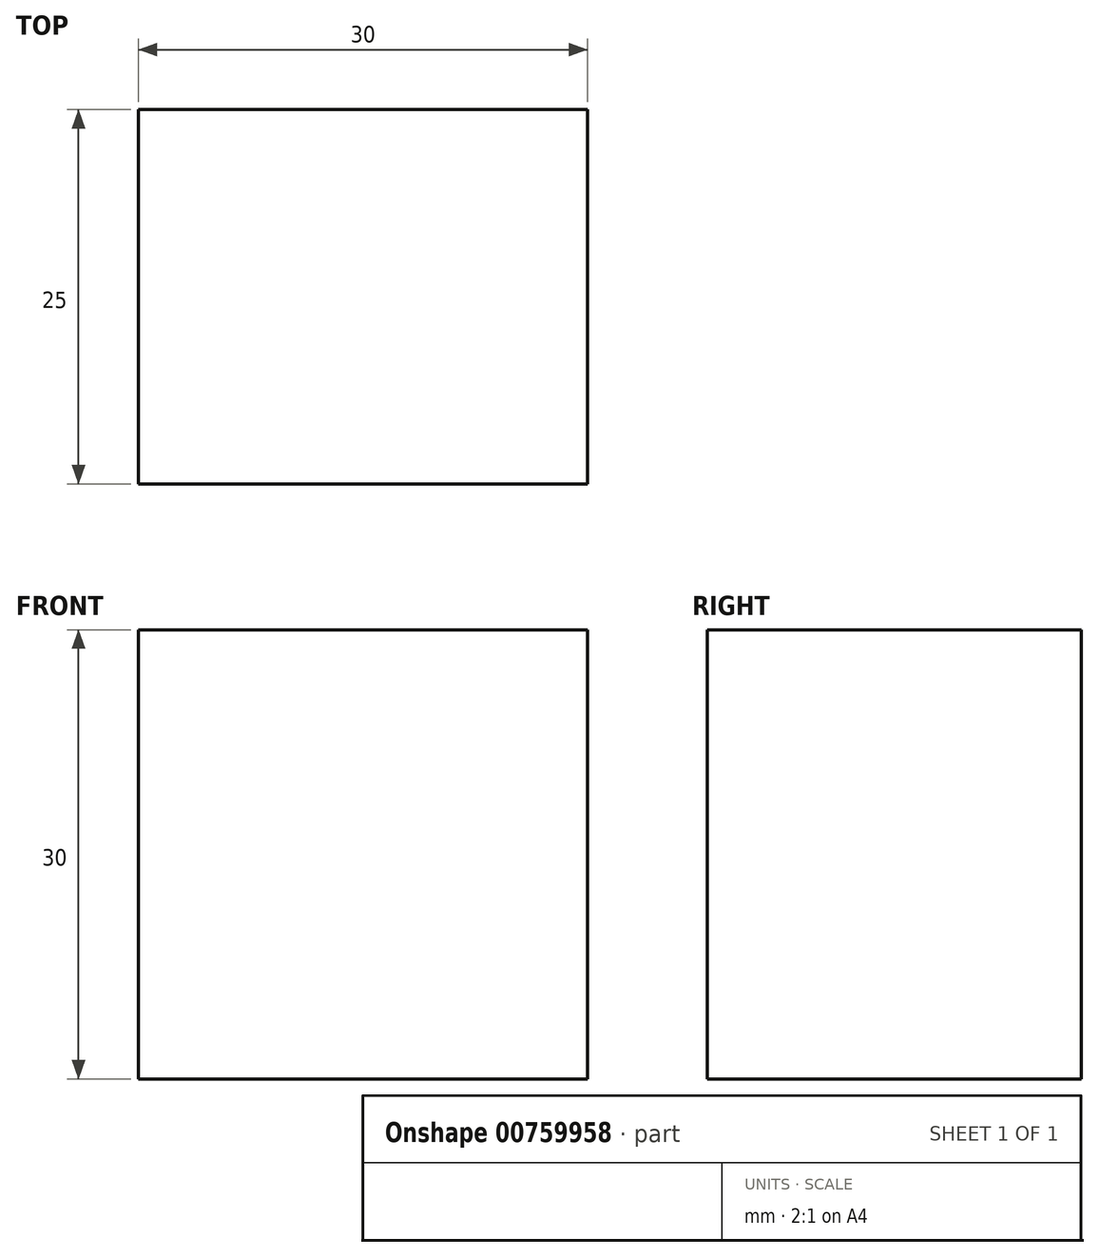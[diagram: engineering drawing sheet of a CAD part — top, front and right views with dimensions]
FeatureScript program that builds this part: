
annotation { "Feature Type Name" : "Feature", "Feature Type Description" : "" }
export const myFeature = defineFeature(function(context is Context, id is Id, definition is map)
    precondition{}
    {
        {
            var Q0;
            Q0=qCreatedBy(makeId("Front.planeOp"),FACE);
            var sketch = newSketch(context, id + "F0", { "sketchPlane" : qUnion([Q0])});
            skLineSegment(sketch, "E0.bottom", {"start": v(-15, 15) * mm, "end": v(15, 15) * mm});
            skLineSegment(sketch, "E0.top", {"start": v(-15, -15) * mm, "end": v(15, -15) * mm});
            skLineSegment(sketch, "E0.left", {"start": v(-15, 15) * mm, "end": v(-15, -15) * mm});
            skLineSegment(sketch, "E0.right", {"start": v(15, 15) * mm, "end": v(15, -15) * mm});
            skPoint(sketch, "E0.middle", {"position": v(0, 0) * mm});
            skSolve(sketch);
        }
        {
            var Q0;
            Q0=makeQuery(id+"F0.imprint","IMPRINT",FACE,{"disambiguationData":[TD([[makeQuery(id+"F0.imprint","IMPRINT",EDGE,{"derivedFrom":sQuery(id+"F0.wireOp",EDGE,"E0.bottom")}),-1.0]])]});
            extrude(context, id + "F1", {"entities" : qUnion([Q0]), "depth" : 25 * mm, "offsetDistance" : 25 * mm});
        }
        {
            var Q0;
            Q0 = qSketchRegion(id + "F0", true);
            extrude(context, id + "F2", {"entities" : qUnion([Q0]), "operationType" : NewBodyOperationType.ADD, "depth" : 25 * mm, "offsetDistance" : 25 * mm});
        }
    });
